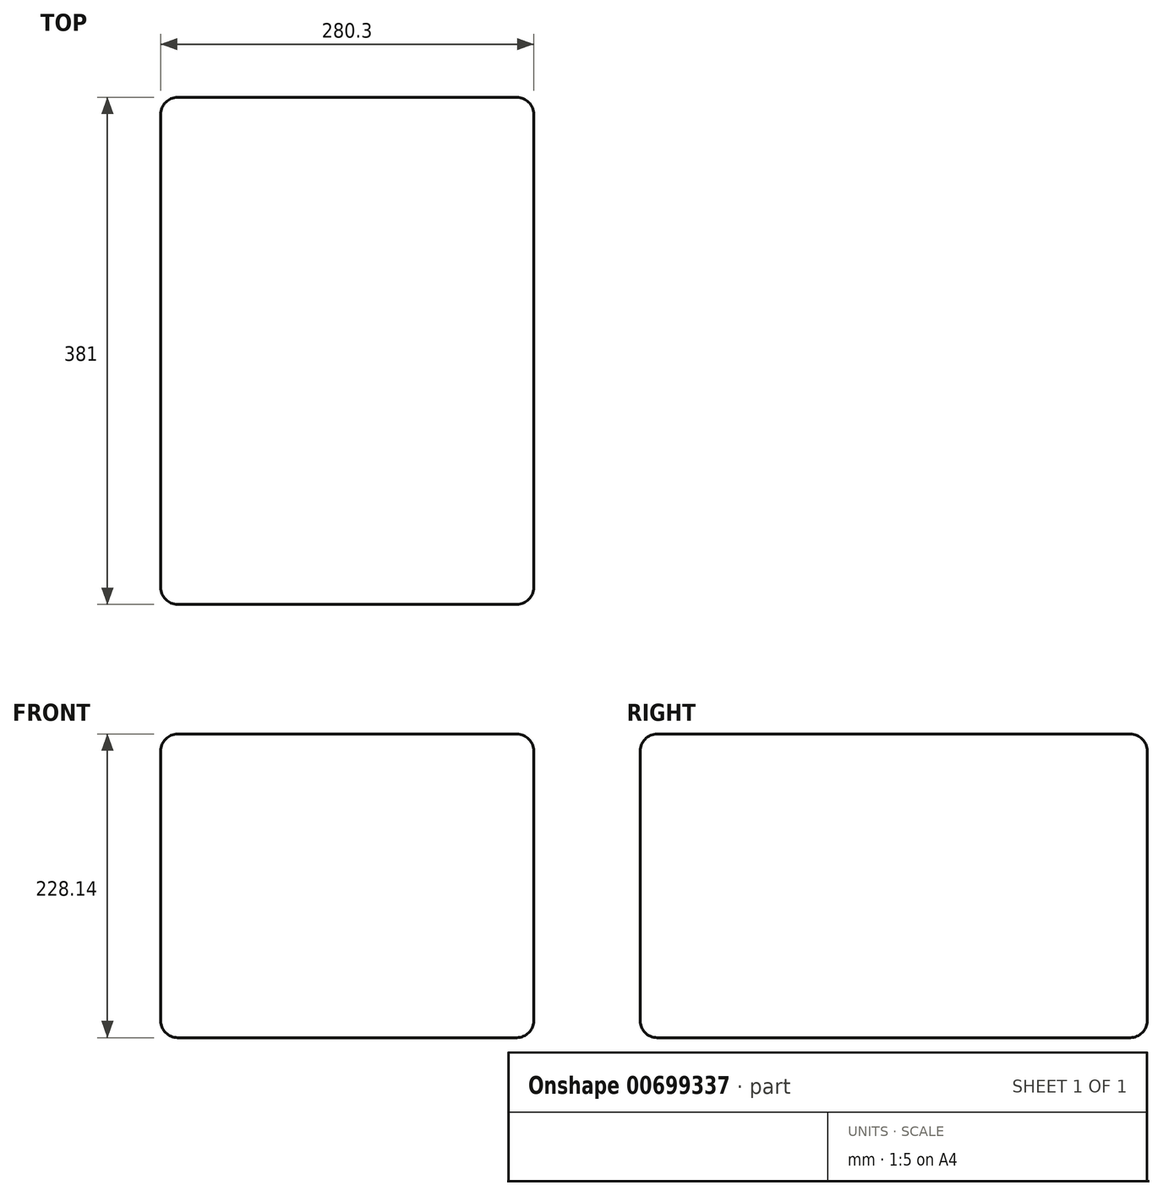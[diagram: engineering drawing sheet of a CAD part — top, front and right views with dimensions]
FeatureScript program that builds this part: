
annotation { "Feature Type Name" : "Feature", "Feature Type Description" : "" }
export const myFeature = defineFeature(function(context is Context, id is Id, definition is map)
    precondition{}
    {
        {
            var Q0;
            Q0=qCreatedBy(makeId("Front.planeOp"),FACE);
            var sketch = newSketch(context, id + "F0", { "sketchPlane" : qUnion([Q0])});
            skLineSegment(sketch, "E0.bottom", {"start": v(140.15, -114.07) * mm, "end": v(-140.15, -114.07) * mm});
            skLineSegment(sketch, "E0.top", {"start": v(140.15, 114.07) * mm, "end": v(-140.15, 114.07) * mm});
            skLineSegment(sketch, "E0.left", {"start": v(140.15, -114.07) * mm, "end": v(140.15, 114.07) * mm});
            skLineSegment(sketch, "E0.right", {"start": v(-140.15, -114.07) * mm, "end": v(-140.15, 114.07) * mm});
            skPoint(sketch, "E0.middle", {"position": v(0, 0) * mm});
            skSolve(sketch);
        }
        {
            var Q0;
            Q0=makeQuery(id+"F0.imprint","IMPRINT",FACE,{"disambiguationData":[TD([[makeQuery(id+"F0.imprint","IMPRINT",EDGE,{"derivedFrom":sQuery(id+"F0.wireOp",EDGE,"E0.bottom")}),-1.0]])]});
            extrude(context, id + "F1", {"entities" : qUnion([Q0]), "depth" : 381 * mm, "offsetDistance" : 25.4 * mm});
        }
        {
            var Q0;
            Q0=makeQuery(id+"F1.opExtrude","CAP_EDGE",EDGE,{"disambiguationData":[OSD([sQuery(id+"F0.wireOp",EDGE,"E0.top")])],"isStart":false});
            fillet(context, id + "F2", {"entities" : qUnion([Q0]), "radius" : 12.7 * mm, "tangentPropagation" : true, "allowEdgeOverflow" : false});
        }
        {
            var Q0;
            Q0=makeQuery(id+"F1.opExtrude","SWEPT_EDGE",EDGE,{"disambiguationData":[OSD([sQuery(id+"F0.wireOp",EDGE,"E0.top"),sQuery(id+"F0.wireOp",EDGE,"E0.left")])]});
            var Q1;
            Q1=makeQuery(id+"F1.opExtrude","CAP_EDGE",EDGE,{"disambiguationData":[OSD([sQuery(id+"F0.wireOp",EDGE,"E0.top")])],"isStart":true});
            var Q2;
            Q2=makeQuery(id+"F1.opExtrude","SWEPT_EDGE",EDGE,{"disambiguationData":[OSD([sQuery(id+"F0.wireOp",EDGE,"E0.top"),sQuery(id+"F0.wireOp",EDGE,"E0.right")])]});
            fillet(context, id + "F3", {"entities" : qUnion([Q0, Q1, Q2]), "radius" : 12.7 * mm, "tangentPropagation" : true, "allowEdgeOverflow" : false});
        }
        {
            var Q0;
            Q0=makeQuery(id+"F1.opExtrude","CAP_EDGE",EDGE,{"disambiguationData":[OSD([sQuery(id+"F0.wireOp",EDGE,"E0.bottom")])],"isStart":true});
            fillet(context, id + "F4", {"entities" : qUnion([Q0]), "radius" : 12.7 * mm, "tangentPropagation" : true, "allowEdgeOverflow" : false});
        }
        {
            var Q0;
            Q0=makeQuery(id+"F1.opExtrude","CAP_EDGE",EDGE,{"disambiguationData":[OSD([sQuery(id+"F0.wireOp",EDGE,"E0.right")])],"isStart":true});
            fillet(context, id + "F5", {"entities" : qUnion([Q0]), "radius" : 12.7 * mm, "tangentPropagation" : true, "allowEdgeOverflow" : false});
        }
    });
